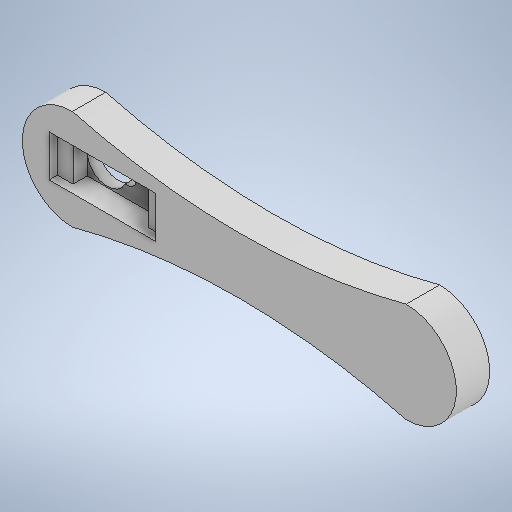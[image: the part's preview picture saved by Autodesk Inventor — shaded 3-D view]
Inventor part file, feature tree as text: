
AUTODESK INVENTOR PART (.ipt)
format: ipt  version: 2025.2 (Build 292293000, 293)  size: 267,264 bytes
history: native  units: mm
features: extrude x4, sketch x4, other x1
ambient origin geometry x8: Origin, YZ Plane, XZ Plane, XY Plane, X Axis, Y Axis, Z Axis, Center Point
bodies: Body1 (feature_tree)
feature tree (9):
  other  "Bryła1"
  extrude  "Wyciągnięcie proste1"  Depth=194.165mm
  extrude  "Wyciągnięcie proste2"  Depth=194.165mm
  extrude  "Wyciągnięcie proste3"  Depth=10.0mm TaperAngle=0.0deg
  extrude  "Wyciągnięcie proste4"  Depth=32.0mm
  sketch  "Szkic1"
  sketch  "Szkic2"
  sketch  "Szkic3"
  sketch  "Szkic4"
